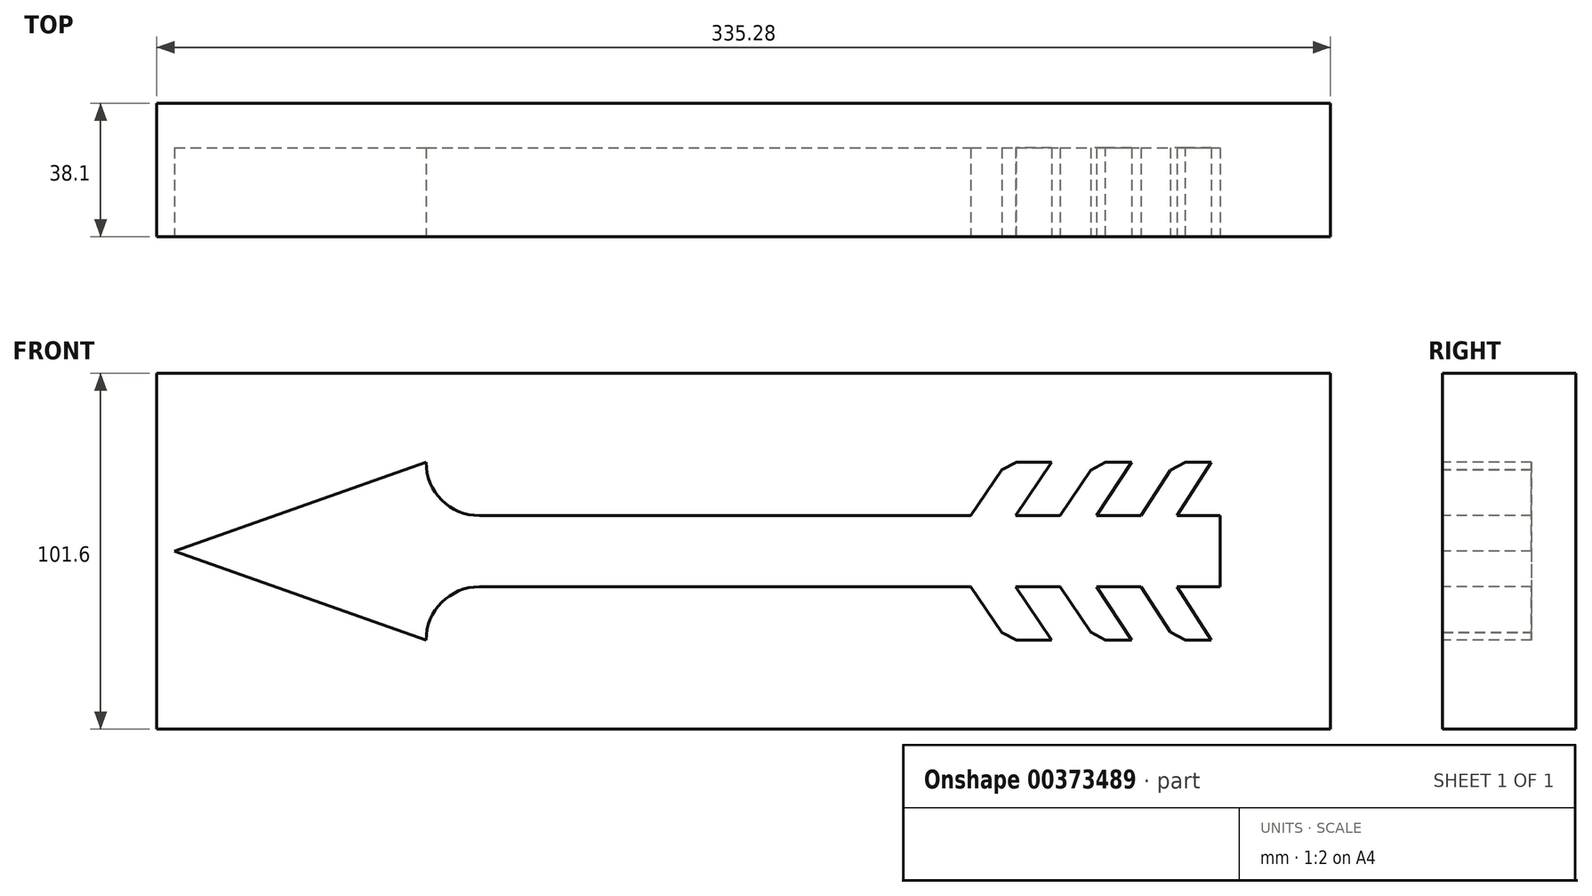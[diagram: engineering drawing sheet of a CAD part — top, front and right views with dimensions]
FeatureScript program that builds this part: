
annotation { "Feature Type Name" : "Feature", "Feature Type Description" : "" }
export const myFeature = defineFeature(function(context is Context, id is Id, definition is map)
    precondition{}
    {
        {
            var Q0;
            Q0=qCreatedBy(makeId("Front.planeOp"),FACE);
            var sketch = newSketch(context, id + "F0", { "sketchPlane" : qUnion([Q0])});
            skLineSegment(sketch, "E0.bottom", {"start": v(-152.4, 25.4) * mm, "end": v(152.4, 25.4) * mm});
            skLineSegment(sketch, "E0.top", {"start": v(-152.4, -25.4) * mm, "end": v(152.4, -25.4) * mm});
            skLineSegment(sketch, "E0.left", {"start": v(-152.4, 25.4) * mm, "end": v(-152.4, -25.4) * mm});
            skLineSegment(sketch, "E0.right", {"start": v(152.4, 25.4) * mm, "end": v(152.4, -25.4) * mm});
            skSolve(sketch);
        }
        {
            var Q0;
            Q0=qSketchRegion(id+"F0",true);
            extrude(context, id + "F1", {"entities" : qUnion([Q0]), "depth" : 38.1 * mm});
        }
        {
            var Q0;
            Q0=makeQuery(id+"F1.opExtrude","SWEPT_FACE",FACE,{"disambiguationData":[OSD([sQuery(id+"F0.wireOp",EDGE,"E0.bottom")])]});
            var sketch = newSketch(context, id + "F2", { "sketchPlane" : qUnion([Q0])});
            skLineSegment(sketch, "E1.bottom", {"start": v(-152.4, -38.1) * mm, "end": v(152.4, -38.1) * mm});
            skLineSegment(sketch, "E1.top", {"start": v(-152.4, 0) * mm, "end": v(152.4, 0) * mm});
            skLineSegment(sketch, "E1.left", {"start": v(-152.4, -38.1) * mm, "end": v(-152.4, 0) * mm});
            skLineSegment(sketch, "E1.right", {"start": v(152.4, -38.1) * mm, "end": v(152.4, 0) * mm});
            skSolve(sketch);
        }
        {
            var Q0;
            Q0 = qSketchRegion(id + "F2", true);
            extrude(context, id + "F3", {"entities" : qUnion([Q0]), "operationType" : NewBodyOperationType.ADD, "depth" : 25.4 * mm});
        }
        {
            var Q0;
            Q0=makeQuery(id+"F1.opExtrude","SWEPT_FACE",FACE,{"disambiguationData":[OSD([sQuery(id+"F0.wireOp",EDGE,"E0.top")])]});
            var sketch = newSketch(context, id + "F4", { "sketchPlane" : qUnion([Q0])});
            skLineSegment(sketch, "E2.bottom", {"start": v(-152.4, 0) * mm, "end": v(152.4, 0) * mm});
            skLineSegment(sketch, "E2.top", {"start": v(-152.4, 38.1) * mm, "end": v(152.4, 38.1) * mm});
            skLineSegment(sketch, "E2.left", {"start": v(-152.4, 0) * mm, "end": v(-152.4, 38.1) * mm});
            skLineSegment(sketch, "E2.right", {"start": v(152.4, 0) * mm, "end": v(152.4, 38.1) * mm});
            skSolve(sketch);
        }
        {
            var Q0;
            Q0 = qSketchRegion(id + "F4", true);
            extrude(context, id + "F5", {"entities" : qUnion([Q0]), "operationType" : NewBodyOperationType.ADD, "depth" : 25.4 * mm});
        }
        {
            var Q0;
            Q0=makeQuery(id+"F5.boolean.opBoolean","MERGE",FACE,{"derivedFrom":[makeQuery(id+"F3.boolean.opBoolean","MERGE",FACE,{"derivedFrom":[makeQuery(id+"F1.opExtrude","SWEPT_FACE",FACE,{"disambiguationData":[OSD([sQuery(id+"F0.wireOp",EDGE,"E0.left")])]}),makeQuery(id+"F3.opExtrude","SWEPT_FACE",FACE,{"disambiguationData":[OSD([sQuery(id+"F2.wireOp",EDGE,"E1.left")])]})]}),makeQuery(id+"F5.opExtrude","SWEPT_FACE",FACE,{"disambiguationData":[OSD([sQuery(id+"F4.wireOp",EDGE,"E2.left")])]})]});
            var sketch = newSketch(context, id + "F6", { "sketchPlane" : qUnion([Q0])});
            skLineSegment(sketch, "E3.bottom", {"start": v(0, 50.8) * mm, "end": v(38.1, 50.8) * mm});
            skLineSegment(sketch, "E3.top", {"start": v(0, -50.8) * mm, "end": v(38.1, -50.8) * mm});
            skLineSegment(sketch, "E3.left", {"start": v(0, 50.8) * mm, "end": v(0, -50.8) * mm});
            skLineSegment(sketch, "E3.right", {"start": v(38.1, 50.8) * mm, "end": v(38.1, -50.8) * mm});
            skSolve(sketch);
        }
        {
            var Q0;
            Q0 = qSketchRegion(id + "F6", true);
            extrude(context, id + "F7", {"entities" : qUnion([Q0]), "operationType" : NewBodyOperationType.ADD, "depth" : 5.08 * mm});
        }
        {
            var Q0;
            Q0=makeQuery(id+"F1.opExtrude","CAP_FACE",FACE,{"disambiguationData":[OSD([sQuery(id+"F0.wireOp",EDGE,"E0.bottom"),sQuery(id+"F0.wireOp",EDGE,"E0.top"),sQuery(id+"F0.wireOp",EDGE,"E0.left"),sQuery(id+"F0.wireOp",EDGE,"E0.right")])],"isStart":false});
            var sketch = newSketch(context, id + "F8", { "sketchPlane" : qUnion([Q0])});
            skLineSegment(sketch, "E4", {"start": v(-152.4, 0) * mm, "end": v(-80.56, 25.4) * mm});
            skLineSegment(sketch, "E5", {"start": v(-80.56, 25.4) * mm, "end": v(-80.56, 10.16) * mm});
            skLineSegment(sketch, "E6", {"start": v(-80.56, 10.16) * mm, "end": v(75.02, 10.16) * mm});
            skLineSegment(sketch, "E7", {"start": v(75.02, 10.16) * mm, "end": v(85.46, 25.4) * mm});
            skLineSegment(sketch, "E8", {"start": v(85.46, 25.4) * mm, "end": v(98.16, 25.4) * mm});
            skLineSegment(sketch, "E9", {"start": v(98.16, 25.4) * mm, "end": v(87.87, 10.16) * mm});
            skLineSegment(sketch, "E10", {"start": v(87.87, 10.16) * mm, "end": v(100.57, 10.16) * mm});
            skLineSegment(sketch, "E11", {"start": v(100.57, 10.16) * mm, "end": v(110.8, 25.4) * mm});
            skLineSegment(sketch, "E12", {"start": v(110.8, 25.4) * mm, "end": v(120.96, 25.4) * mm});
            skLineSegment(sketch, "E13", {"start": v(120.96, 25.4) * mm, "end": v(110.92, 10.16) * mm});
            skLineSegment(sketch, "E14", {"start": v(110.92, 10.16) * mm, "end": v(123.62, 10.16) * mm});
            skLineSegment(sketch, "E15", {"start": v(123.62, 10.16) * mm, "end": v(133.6, 25.4) * mm});
            skLineSegment(sketch, "E16", {"start": v(133.6, 25.4) * mm, "end": v(143.76, 25.4) * mm});
            skLineSegment(sketch, "E17", {"start": v(143.76, 25.4) * mm, "end": v(133.97, 10.16) * mm});
            skLineSegment(sketch, "E18", {"start": v(133.97, 10.16) * mm, "end": v(146.24, 10.16) * mm});
            skLineSegment(sketch, "E19", {"start": v(146.24, 10.16) * mm, "end": v(146.24, 0) * mm});
            skLineSegment(sketch, "E20", {"start": v(-152.4, 0) * mm, "end": v(146.24, 0) * mm});
            skLineSegment(sketch, "E21.MirrorCS", {"start": v(-80.56, -10.16) * mm, "end": v(75.02, -10.16) * mm});
            skLineSegment(sketch, "E22.MirrorCS", {"start": v(-80.56, -25.4) * mm, "end": v(-80.56, -10.16) * mm});
            skLineSegment(sketch, "E23.MirrorCS", {"start": v(-152.4, 0) * mm, "end": v(-80.56, -25.4) * mm});
            skLineSegment(sketch, "E24.MirrorCS", {"start": v(75.02, -10.16) * mm, "end": v(85.46, -25.4) * mm});
            skLineSegment(sketch, "E25.MirrorCS", {"start": v(98.16, -25.4) * mm, "end": v(87.87, -10.16) * mm});
            skLineSegment(sketch, "E26.MirrorCS", {"start": v(100.57, -10.16) * mm, "end": v(110.8, -25.4) * mm});
            skLineSegment(sketch, "E27.MirrorCS", {"start": v(120.96, -25.4) * mm, "end": v(110.92, -10.16) * mm});
            skLineSegment(sketch, "E28.MirrorCS", {"start": v(123.62, -10.16) * mm, "end": v(133.6, -25.4) * mm});
            skLineSegment(sketch, "E29.MirrorCS", {"start": v(143.76, -25.4) * mm, "end": v(133.97, -10.16) * mm});
            skLineSegment(sketch, "E30.MirrorCS", {"start": v(146.24, -10.16) * mm, "end": v(146.24, 0) * mm});
            skLineSegment(sketch, "E31.MirrorCS", {"start": v(133.97, -10.16) * mm, "end": v(146.24, -10.16) * mm});
            skLineSegment(sketch, "E32.MirrorCS", {"start": v(87.87, -10.16) * mm, "end": v(100.57, -10.16) * mm});
            skLineSegment(sketch, "E33.MirrorCS", {"start": v(110.92, -10.16) * mm, "end": v(123.62, -10.16) * mm});
            skLineSegment(sketch, "E34", {"start": v(75.02, 10.16) * mm, "end": v(87.87, 10.16) * mm});
            skLineSegment(sketch, "E35", {"start": v(123.62, 10.16) * mm, "end": v(133.97, 10.16) * mm});
            skLineSegment(sketch, "E36", {"start": v(100.57, 10.16) * mm, "end": v(110.92, 10.16) * mm});
            skLineSegment(sketch, "E37.MirrorCS", {"start": v(75.02, -10.16) * mm, "end": v(87.87, -10.16) * mm});
            skLineSegment(sketch, "E38.MirrorCS", {"start": v(100.57, -10.16) * mm, "end": v(110.92, -10.16) * mm});
            skLineSegment(sketch, "E39.MirrorCS", {"start": v(123.62, -10.16) * mm, "end": v(133.97, -10.16) * mm});
            skLineSegment(sketch, "E40", {"start": v(85.46, -25.4) * mm, "end": v(98.16, -25.4) * mm});
            skLineSegment(sketch, "E41", {"start": v(110.8, -25.4) * mm, "end": v(120.96, -25.4) * mm});
            skLineSegment(sketch, "E42", {"start": v(133.6, -25.4) * mm, "end": v(143.76, -25.4) * mm});
            skSolve(sketch);
        }
        {
            var Q0;
            Q0=makeQuery(id+"F8.imprint","IMPRINT",FACE,{"disambiguationData":[TD([[makeQuery(id+"F8.imprint","IMPRINT",EDGE,{"derivedFrom":sQuery(id+"F8.wireOp",EDGE,"E4")}),-1.0]])]});
            var Q1;
            Q1=makeQuery(id+"F8.imprint","IMPRINT",FACE,{"disambiguationData":[TD([[makeQuery(id+"F8.imprint","IMPRINT",EDGE,{"derivedFrom":sQuery(id+"F8.wireOp",EDGE,"E20")}),-1.0]])]});
            var Q2;
            Q2=makeQuery(id+"F8.imprint","IMPRINT",FACE,{"disambiguationData":[TD([[makeQuery(id+"F8.imprint","IMPRINT",EDGE,{"derivedFrom":sQuery(id+"F8.wireOp",EDGE,"E7")}),-1.0]])]});
            var Q3;
            Q3=makeQuery(id+"F8.imprint","IMPRINT",FACE,{"disambiguationData":[TD([[makeQuery(id+"F8.imprint","IMPRINT",EDGE,{"derivedFrom":sQuery(id+"F8.wireOp",EDGE,"E11")}),-1.0]])]});
            var Q4;
            Q4=makeQuery(id+"F8.imprint","IMPRINT",FACE,{"disambiguationData":[TD([[makeQuery(id+"F8.imprint","IMPRINT",EDGE,{"derivedFrom":sQuery(id+"F8.wireOp",EDGE,"E15")}),-1.0]])]});
            var Q5;
            Q5=makeQuery(id+"F8.imprint","IMPRINT",FACE,{"disambiguationData":[TD([[makeQuery(id+"F8.imprint","IMPRINT",EDGE,{"derivedFrom":sQuery(id+"F8.wireOp",EDGE,"E28.MirrorCS")}),1.0]])]});
            var Q6;
            Q6=makeQuery(id+"F8.imprint","IMPRINT",FACE,{"disambiguationData":[TD([[makeQuery(id+"F8.imprint","IMPRINT",EDGE,{"derivedFrom":sQuery(id+"F8.wireOp",EDGE,"E26.MirrorCS")}),1.0]])]});
            var Q7;
            Q7=makeQuery(id+"F8.imprint","IMPRINT",FACE,{"disambiguationData":[TD([[makeQuery(id+"F8.imprint","IMPRINT",EDGE,{"derivedFrom":sQuery(id+"F8.wireOp",EDGE,"E24.MirrorCS")}),1.0]])]});
            extrude(context, id + "F9", {"entities" : qUnion([Q0, Q1, Q2, Q3, Q4, Q5, Q6, Q7]), "operationType" : NewBodyOperationType.REMOVE, "oppositeDirection" : true, "depth" : 25.4 * mm});
        }
        {
            var Q0;
            Q0=makeQuery(id+"F9.boolean.opBoolean","COPY",EDGE,{"derivedFrom":makeQuery(id+"F9.opExtrude","SWEPT_EDGE",EDGE,{"disambiguationData":[OSD([sQuery(id+"F8.wireOp",EDGE,"E22.MirrorCS"),sQuery(id+"F8.wireOp",EDGE,"E21.MirrorCS")])]})});
            var Q1;
            Q1=makeQuery(id+"F9.boolean.opBoolean","COPY",EDGE,{"derivedFrom":makeQuery(id+"F9.opExtrude","SWEPT_EDGE",EDGE,{"disambiguationData":[OSD([sQuery(id+"F8.wireOp",EDGE,"E5"),sQuery(id+"F8.wireOp",EDGE,"E6")])]})});
            fillet(context, id + "F10", {"entities" : qUnion([Q0, Q1]), "radius" : 15.24 * mm, "tangentPropagation" : true, "allowEdgeOverflow" : false});
        }
        {
            var Q0;
            Q0=makeQuery(id+"F9.boolean.opBoolean","COPY",EDGE,{"derivedFrom":makeQuery(id+"F9.opExtrude","SWEPT_EDGE",EDGE,{"disambiguationData":[OSD([sQuery(id+"F0.wireOp",EDGE,"E0.top"),sQuery(id+"F8.wireOp",EDGE,"E24.MirrorCS")])]})});
            var Q1;
            Q1=makeQuery(id+"F9.boolean.opBoolean","COPY",EDGE,{"derivedFrom":makeQuery(id+"F9.opExtrude","SWEPT_EDGE",EDGE,{"disambiguationData":[OSD([sQuery(id+"F0.wireOp",EDGE,"E0.top"),sQuery(id+"F8.wireOp",EDGE,"E26.MirrorCS")])]})});
            var Q2;
            Q2=makeQuery(id+"F9.boolean.opBoolean","COPY",EDGE,{"derivedFrom":makeQuery(id+"F9.opExtrude","SWEPT_EDGE",EDGE,{"disambiguationData":[OSD([sQuery(id+"F0.wireOp",EDGE,"E0.top"),sQuery(id+"F8.wireOp",EDGE,"E28.MirrorCS")])]})});
            var Q3;
            Q3=makeQuery(id+"F9.boolean.opBoolean","COPY",EDGE,{"derivedFrom":makeQuery(id+"F9.opExtrude","SWEPT_EDGE",EDGE,{"disambiguationData":[OSD([sQuery(id+"F0.wireOp",EDGE,"E0.bottom"),sQuery(id+"F8.wireOp",EDGE,"E15"),sQuery(id+"F8.wireOp",EDGE,"E16")])]})});
            var Q4;
            Q4=makeQuery(id+"F9.boolean.opBoolean","COPY",EDGE,{"derivedFrom":makeQuery(id+"F9.opExtrude","SWEPT_EDGE",EDGE,{"disambiguationData":[OSD([sQuery(id+"F0.wireOp",EDGE,"E0.bottom"),sQuery(id+"F8.wireOp",EDGE,"E11"),sQuery(id+"F8.wireOp",EDGE,"E12")])]})});
            var Q5;
            Q5=makeQuery(id+"F9.boolean.opBoolean","COPY",EDGE,{"derivedFrom":makeQuery(id+"F9.opExtrude","SWEPT_EDGE",EDGE,{"disambiguationData":[OSD([sQuery(id+"F0.wireOp",EDGE,"E0.bottom"),sQuery(id+"F8.wireOp",EDGE,"E7"),sQuery(id+"F8.wireOp",EDGE,"E8")])]})});
            chamfer(context, id + "F11", {"entities" : qUnion([Q0, Q1, Q2, Q3, Q4, Q5]), "width" : 5.08 * mm, "tangentPropagation" : true});
        }
        {
            var Q0;
            Q0=makeQuery(id+"FqULFja6iJfG4bt_1.boolean.opBoolean","MERGE",FACE,{"derivedFrom":[makeQuery(id+"FnmqDjYCesAkyfp_1.boolean.opBoolean","MERGE",FACE,{"derivedFrom":[makeQuery(id+"F1.opExtrude","SWEPT_FACE",FACE,{"disambiguationData":[OSD([sQuery(id+"F0.wireOp",EDGE,"E0.right")])]}),makeQuery(id+"FnmqDjYCesAkyfp_1.opExtrude","SWEPT_FACE",FACE,{"disambiguationData":[OSD([sQuery(id+"FBsOIoBMVGm8epH_1.wireOp",EDGE,"e4tsU5Ny-pqJD-BhK3-DdSg-fcs7NWUB6jc0")])]})]}),makeQuery(id+"FqULFja6iJfG4bt_1.opExtrude","SWEPT_FACE",FACE,{"disambiguationData":[OSD([sQuery(id+"FlILKnTmFWEWQAo_1.wireOp",EDGE,"mNPD4qg8-OHSR-dsEh-miyK-SrQP7sBlWkq6")])]})]});
            extrude(context, id + "F12", {"entities" : qUnion([Q0]), "operationType" : NewBodyOperationType.ADD, "depth" : 25.4 * mm});
        }
    });
